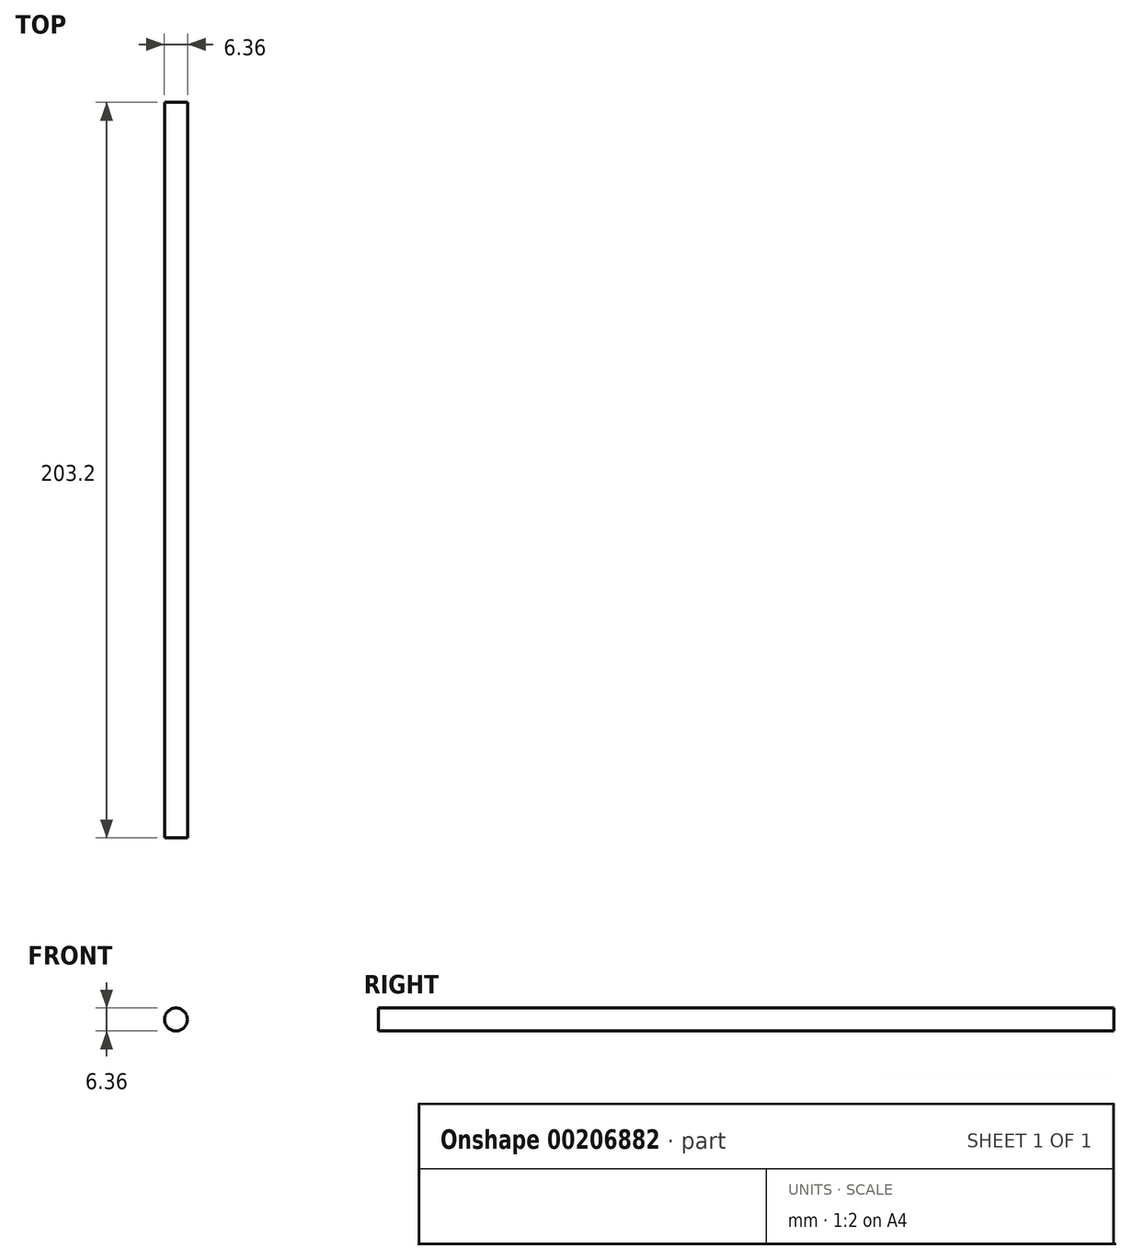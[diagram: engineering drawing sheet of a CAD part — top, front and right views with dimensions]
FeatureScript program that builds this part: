
annotation { "Feature Type Name" : "Feature", "Feature Type Description" : "" }
export const myFeature = defineFeature(function(context is Context, id is Id, definition is map)
    precondition{}
    {
        {
            var Q0;
            Q0=qCreatedBy(makeId("Front.planeOp"),FACE);
            var sketch = newSketch(context, id + "F0", { "sketchPlane" : qUnion([Q0])});
            skCircle(sketch, "E0", {"center": v(0, 0) * mm, "radius": 3.18 * mm});
            skSolve(sketch);
        }
        {
            var Q0;
            Q0=qSketchRegion(id+"F0",true);
            extrude(context, id + "F1", {"entities" : qUnion([Q0]), "endBound" : BoundingType.SYMMETRIC, "depth" : 203.2 * mm});
        }
    });
